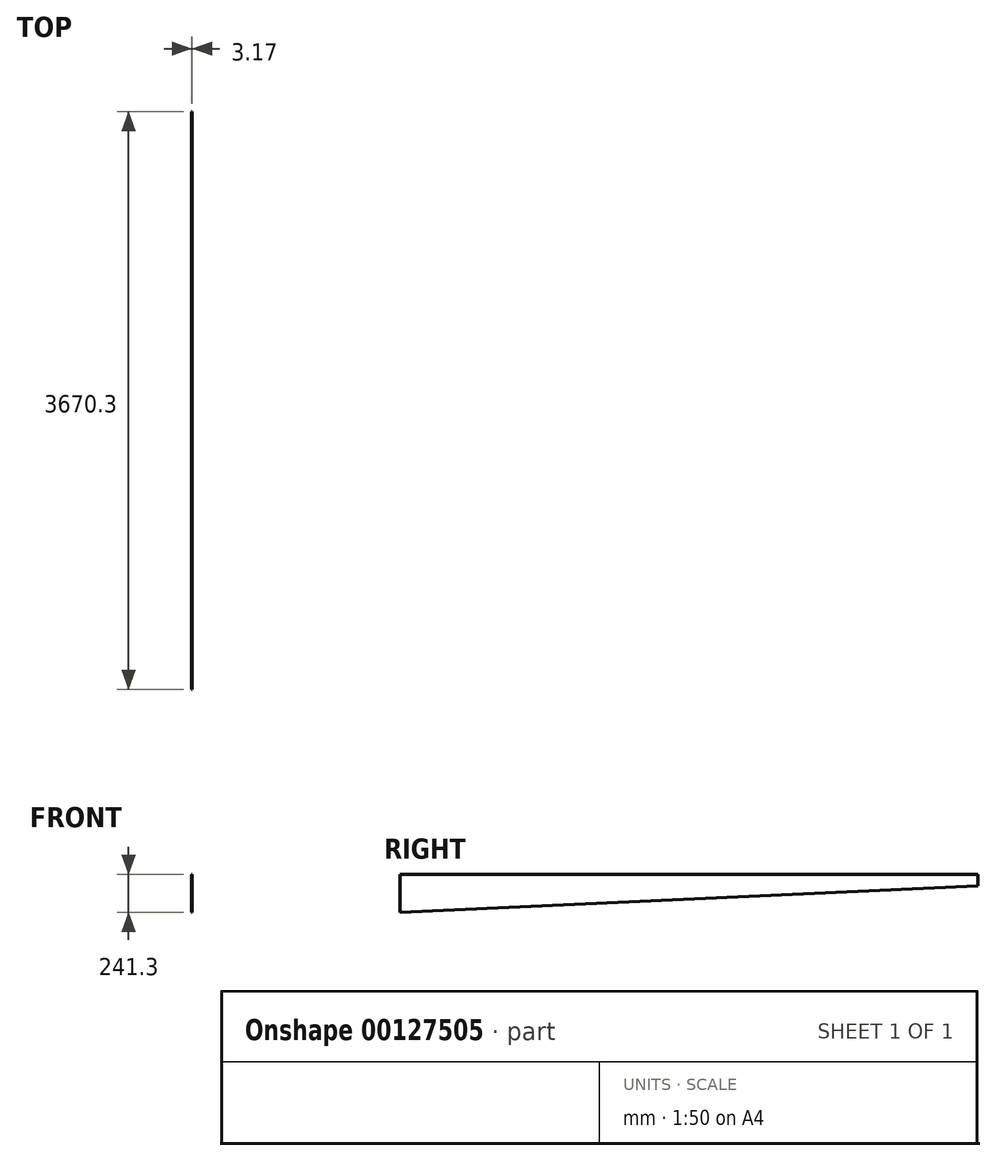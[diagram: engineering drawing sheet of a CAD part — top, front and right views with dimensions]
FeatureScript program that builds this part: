
annotation { "Feature Type Name" : "Feature", "Feature Type Description" : "" }
export const myFeature = defineFeature(function(context is Context, id is Id, definition is map)
    precondition{}
    {
        {
            var Q0;
            Q0=qCreatedBy(makeId("Right.planeOp"),FACE);
            var sketch = newSketch(context, id + "F0", { "sketchPlane" : qUnion([Q0])});
            skLineSegment(sketch, "E0", {"start": v(0, 0) * mm, "end": v(0, -241.3) * mm});
            skLineSegment(sketch, "E1", {"start": v(0, -241.3) * mm, "end": v(3670.3, -72.23) * mm});
            skLineSegment(sketch, "E2", {"start": v(3670.3, -72.23) * mm, "end": v(3670.3, 0) * mm});
            skLineSegment(sketch, "E3", {"start": v(3670.3, 0) * mm, "end": v(0, 0) * mm});
            skSolve(sketch);
        }
        {
            var Q0;
            Q0 = qSketchRegion(id + "F0", true);
            extrude(context, id + "F1", {"entities" : qUnion([Q0]), "depth" : 3.17 * mm});
        }
        {
            var Q0;
            Q0=makeQuery(id+"F1.opExtrude","SWEPT_BODY",BODY,{"disambiguationData":[OSD([sQuery(id+"F0.wireOp",EDGE,"E0"),sQuery(id+"F0.wireOp",EDGE,"E1"),sQuery(id+"F0.wireOp",EDGE,"E2"),sQuery(id+"F0.wireOp",EDGE,"E3")])]});
            transform(context, id + "F2", {"entities" : qUnion([Q0]), "transformType" : TransformType.TRANSLATION_3D, "dx" : 0 * mm, "dy" : 0 * mm, "dz" : 0 * mm, "makeCopy" : true});
        }
    });
